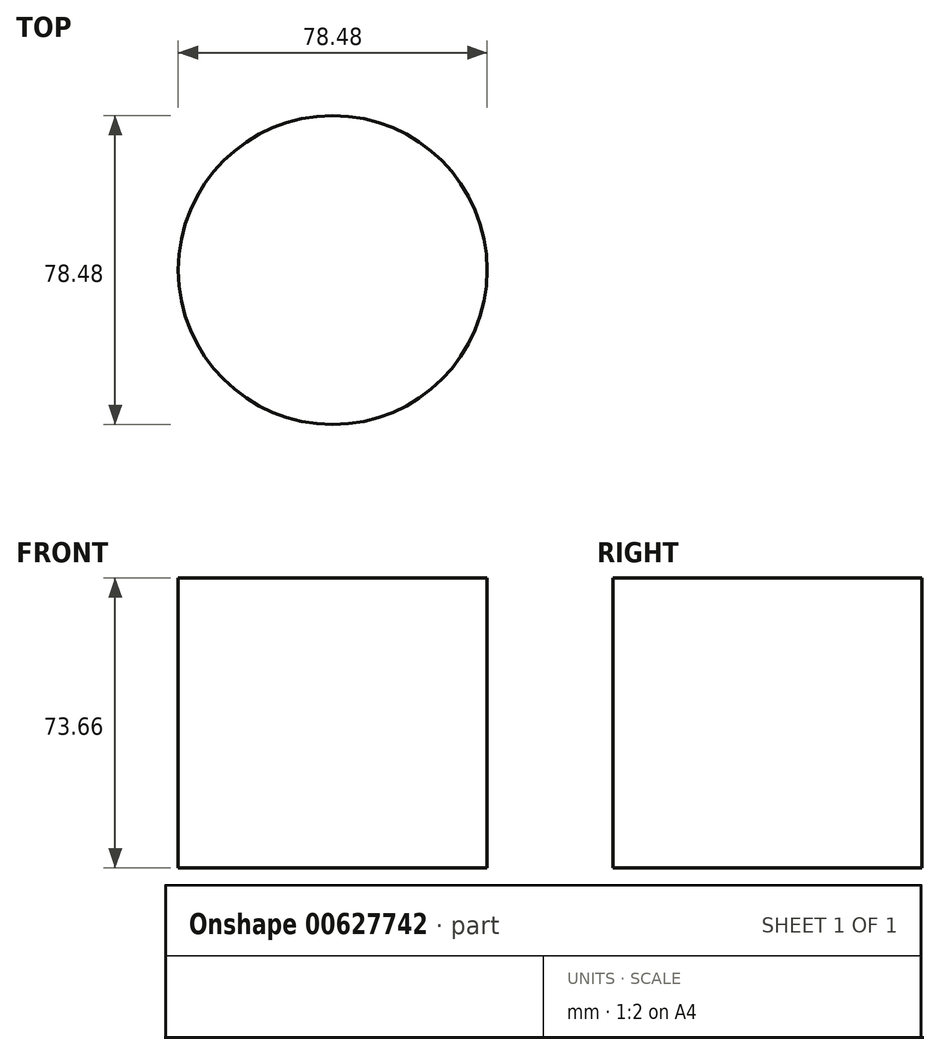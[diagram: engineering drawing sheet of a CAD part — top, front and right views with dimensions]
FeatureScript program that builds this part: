
annotation { "Feature Type Name" : "Feature", "Feature Type Description" : "" }
export const myFeature = defineFeature(function(context is Context, id is Id, definition is map)
    precondition{}
    {
        {
            var Q0;
            Q0=qCreatedBy(makeId("Top.planeOp"),FACE);
            var sketch = newSketch(context, id + "F0", { "sketchPlane" : qUnion([Q0])});
            skCircle(sketch, "E0", {"center": v(0, 0) * mm, "radius": 39.24 * mm});
            skSolve(sketch);
        }
        {
            var Q0;
            Q0=makeQuery(id+"F0.imprint","IMPRINT",FACE,{"disambiguationData":[TD([[makeQuery(id+"F0.imprint","IMPRINT",EDGE,{"derivedFrom":sQuery(id+"F0.wireOp",EDGE,"E0")}),1.0]])]});
            extrude(context, id + "F1", {"entities" : qUnion([Q0]), "depth" : 73.66 * mm, "offsetDistance" : 25.4 * mm});
        }
    });
